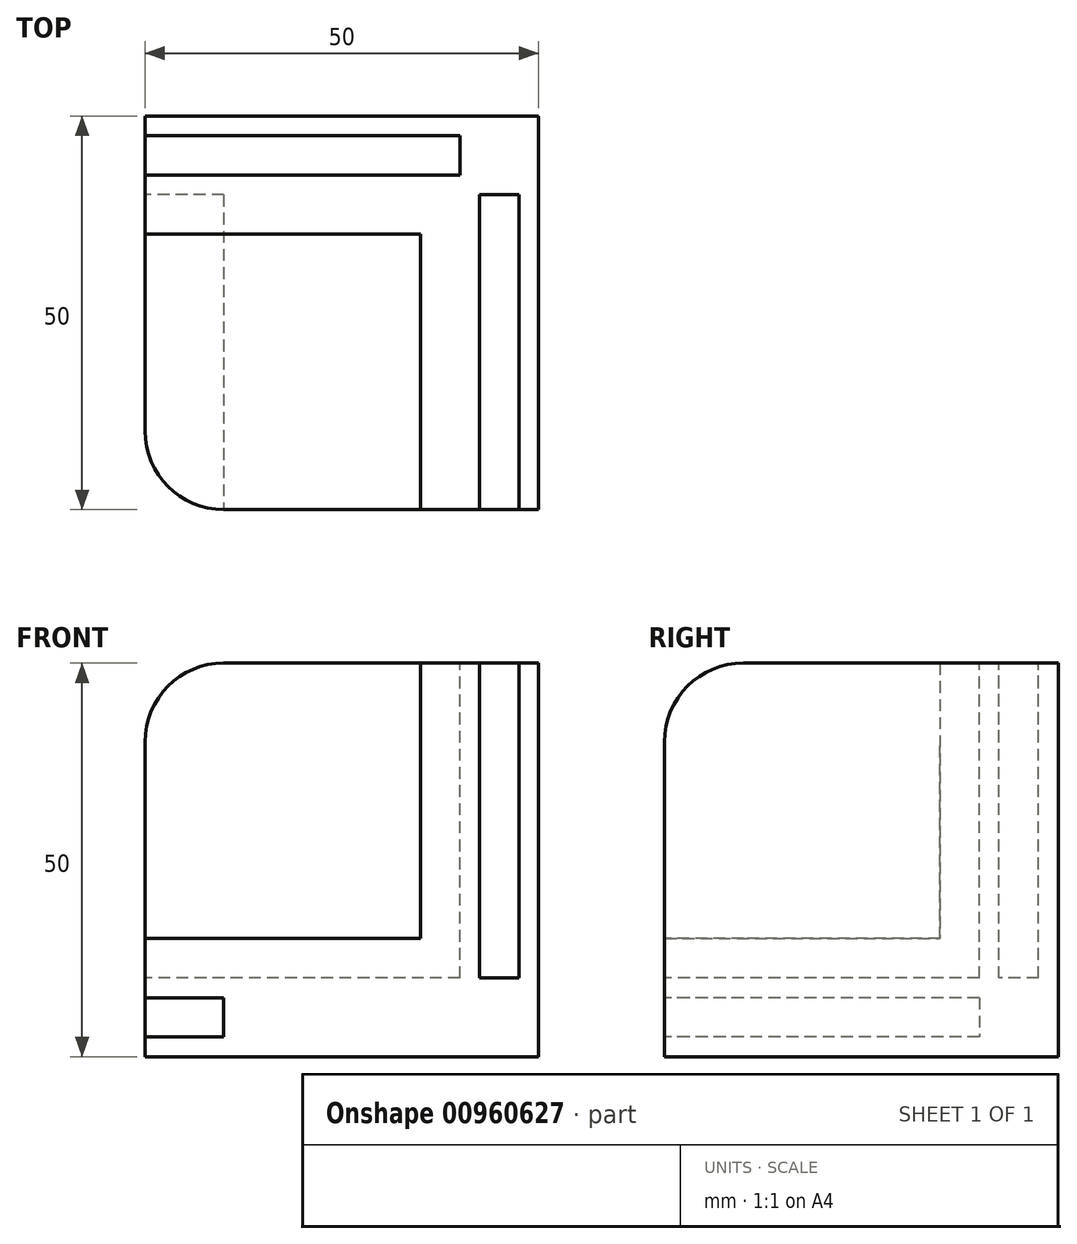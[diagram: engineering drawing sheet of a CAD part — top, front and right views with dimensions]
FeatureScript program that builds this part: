
annotation { "Feature Type Name" : "Feature", "Feature Type Description" : "" }
export const myFeature = defineFeature(function(context is Context, id is Id, definition is map)
    precondition{}
    {
        {
            var Q0;
            Q0=qCreatedBy(makeId("Top.planeOp"),FACE);
            var sketch = newSketch(context, id + "F0", { "sketchPlane" : qUnion([Q0])});
            skLineSegment(sketch, "E0.bottom", {"start": v(0, 0) * mm, "end": v(-50, 0) * mm});
            skLineSegment(sketch, "E0.top", {"start": v(0, -50) * mm, "end": v(-40, -50) * mm});
            skLineSegment(sketch, "E0.left", {"start": v(0, 0) * mm, "end": v(0, -50) * mm});
            skLineSegment(sketch, "E0.right", {"start": v(-50, 0) * mm, "end": v(-50, -40) * mm});
            skPoint(sketch, "E1.visualSharp", {"position": v(-50, -50) * mm});
            skArc(sketch, "E1.filletArc", {"start": v(-50, -40) * mm, "mid": v(-47.07, -47.07) * mm, "end": v(-40, -50) * mm});
            skSolve(sketch);
        }
        {
            var Q0;
            Q0=makeQuery(id+"F0.imprint","IMPRINT",FACE,{"disambiguationData":[TD([[makeQuery(id+"F0.imprint","IMPRINT",EDGE,{"derivedFrom":sQuery(id+"F0.wireOp",EDGE,"tNkWgY0K-5FoM-fzsk-HCrw-KOSka2LcS9h1.bottom")}),-1.0]])]});
            var Q1;
            Q1=makeQuery(id+"F0.imprint","IMPRINT",FACE,{"disambiguationData":[TD([[makeQuery(id+"F0.imprint","IMPRINT",EDGE,{"derivedFrom":sQuery(id+"F0.wireOp",EDGE,"E0.bottom")}),1.0]])]});
            var Q2;
            Q2=makeQuery(id+"F0.imprint","IMPRINT",FACE,{"disambiguationData":[TD([[makeQuery(id+"F0.imprint","IMPRINT",EDGE,{"derivedFrom":sQuery(id+"F0.wireOp",EDGE,"E0.top")}),-1.0]])]});
            var Q3;
            Q3=makeQuery(id+"F0.imprint","IMPRINT",FACE,{"disambiguationData":[TD([[makeQuery(id+"F0.imprint","IMPRINT",EDGE,{"derivedFrom":sQuery(id+"F0.wireOp",EDGE,"fvIwUqZD-S5C8-yHxi-N0ak-uGxWySerV2bo.bottom")}),1.0]])]});
            var Q4;
            Q4=makeQuery(id+"F0.imprint","IMPRINT",FACE,{"disambiguationData":[TD([[makeQuery(id+"F0.imprint","IMPRINT",EDGE,{"derivedFrom":sQuery(id+"F0.wireOp",EDGE,"JSCxDXyh-nDxv-V0qH-dKlW-7TGNpykFalIj.bottom")}),1.0]])]});
            extrude(context, id + "F1", {"entities" : qUnion([Q0, Q1, Q2, Q3, Q4]), "depth" : 15 * mm, "offsetDistance" : 25 * mm});
        }
        {
            var Q0;
            Q0=qCreatedBy(makeId("Right.planeOp"),FACE);
            var sketch = newSketch(context, id + "F2", { "sketchPlane" : qUnion([Q0])});
            skLineSegment(sketch, "E2.bottom", {"start": v(0, 10) * mm, "end": v(-50, 10) * mm});
            skLineSegment(sketch, "E2.top", {"start": v(0, 50) * mm, "end": v(-40, 50) * mm});
            skLineSegment(sketch, "E2.left", {"start": v(0, 10) * mm, "end": v(0, 50) * mm});
            skLineSegment(sketch, "E2.right", {"start": v(-50, 10) * mm, "end": v(-50, 40) * mm});
            skPoint(sketch, "E3.visualSharp", {"position": v(-50, 50) * mm});
            skArc(sketch, "E3.filletArc", {"start": v(-40, 50) * mm, "mid": v(-47.07, 47.07) * mm, "end": v(-50, 40) * mm});
            skSolve(sketch);
        }
        {
            var Q0;
            Q0=makeQuery(id+"F2.imprint","IMPRINT",FACE,{"disambiguationData":[TD([[makeQuery(id+"F2.imprint","IMPRINT",EDGE,{"derivedFrom":sQuery(id+"F2.wireOp",EDGE,"E2.bottom")}),-1.0]])]});
            extrude(context, id + "F3", {"entities" : qUnion([Q0]), "operationType" : NewBodyOperationType.ADD, "oppositeDirection" : true, "depth" : 15 * mm, "offsetDistance" : 25 * mm});
        }
        {
            var Q0;
            Q0=qCreatedBy(makeId("Front.planeOp"),FACE);
            var sketch = newSketch(context, id + "F4", { "sketchPlane" : qUnion([Q0])});
            skLineSegment(sketch, "E4.bottom", {"start": v(-10, 10) * mm, "end": v(-50, 10) * mm});
            skLineSegment(sketch, "E4.top", {"start": v(-10, 50) * mm, "end": v(-40, 50) * mm});
            skLineSegment(sketch, "E4.left", {"start": v(-10, 10) * mm, "end": v(-10, 50) * mm});
            skLineSegment(sketch, "E4.right", {"start": v(-50, 10) * mm, "end": v(-50, 40) * mm});
            skPoint(sketch, "E5.visualSharp", {"position": v(-50, 50) * mm});
            skArc(sketch, "E5.filletArc", {"start": v(-40, 50) * mm, "mid": v(-47.07, 47.07) * mm, "end": v(-50, 40) * mm});
            skSolve(sketch);
        }
        {
            var Q0;
            Q0=makeQuery(id+"F4.imprint","IMPRINT",FACE,{"disambiguationData":[TD([[makeQuery(id+"F4.imprint","IMPRINT",EDGE,{"derivedFrom":sQuery(id+"F4.wireOp",EDGE,"E4.bottom")}),-1.0]])]});
            extrude(context, id + "F5", {"entities" : qUnion([Q0]), "operationType" : NewBodyOperationType.ADD, "depth" : 15 * mm, "offsetDistance" : 25 * mm});
        }
        {
            var Q0;
            Q0=makeQuery(id+"F3.boolean.opBoolean","MERGE",FACE,{"derivedFrom":[makeQuery(id+"F1.opExtrude","SWEPT_FACE",FACE,{"disambiguationData":[OSD([sQuery(id+"F0.wireOp",EDGE,"E0.top")])]}),makeQuery(id+"F3.opExtrude","SWEPT_FACE",FACE,{"disambiguationData":[OSD([sQuery(id+"F2.wireOp",EDGE,"E2.right")])]})]});
            var sketch = newSketch(context, id + "F6", { "sketchPlane" : qUnion([Q0])});
            skLineSegment(sketch, "E6.bottom", {"start": v(-10, 2.5) * mm, "end": v(-60, 2.5) * mm});
            skLineSegment(sketch, "E6.top", {"start": v(-10, 7.5) * mm, "end": v(-60, 7.5) * mm});
            skLineSegment(sketch, "E6.left", {"start": v(-10, 2.5) * mm, "end": v(-10, 7.5) * mm});
            skLineSegment(sketch, "E6.right", {"start": v(-60, 2.5) * mm, "end": v(-60, 7.5) * mm});
            skLineSegment(sketch, "E7.bottom", {"start": v(-10, 2.5) * mm, "end": v(-15, 2.5) * mm});
            skLineSegment(sketch, "E7.top", {"start": v(-10, 52.5) * mm, "end": v(-15, 52.5) * mm});
            skLineSegment(sketch, "E8.bottom", {"start": v(-2.5, 10) * mm, "end": v(-7.5, 10) * mm});
            skLineSegment(sketch, "E8.top", {"start": v(-2.5, 60) * mm, "end": v(-7.5, 60) * mm});
            skLineSegment(sketch, "E8.left", {"start": v(-2.5, 10) * mm, "end": v(-2.5, 60) * mm});
            skLineSegment(sketch, "E8.right", {"start": v(-7.5, 10) * mm, "end": v(-7.5, 60) * mm});
            skSolve(sketch);
        }
        {
            var Q0;
            {var subQ5=sQuery(id+"F6.wireOp",EDGE,"E7.bottom");Q0=makeQuery(id+"F6.imprint","IMPRINT",FACE,{"disambiguationData":[TD([[makeQuery(id+"F6.imprint","IMPRINT",EDGE,{"derivedFrom":subQ5}),-1.0]])]});}
            var Q1;
            {var subQ0=sQuery(id+"F6.wireOp",EDGE,"E7.right");var subQ5=sQuery(id+"F6.wireOp",EDGE,"E6.top");var subQ7=makeQuery(id+"F6.imprint","INTERSECT",VERTEX,{"derivedFrom":[subQ5,subQ0]});Q1=makeQuery(id+"F6.imprint","IMPRINT",FACE,{"disambiguationData":[TD([[makeQuery(id+"F6.imprint","IMPRINT",EDGE,{"disambiguationData":[TD([[subQ7,-1.0]])],"derivedFrom":subQ5}),1.0]])]});}
            var Q2;
            {var subQ0=sQuery(id+"F6.wireOp",EDGE,"E6.right");Q2=makeQuery(id+"F6.imprint","IMPRINT",FACE,{"disambiguationData":[TD([[makeQuery(id+"F6.imprint","IMPRINT",EDGE,{"derivedFrom":subQ0}),-1.0]])]});}
            var Q3;
            {var subQ0=sQuery(id+"F6.wireOp",EDGE,"E8.bottom");Q3=makeQuery(id+"F6.imprint","IMPRINT",FACE,{"disambiguationData":[TD([[makeQuery(id+"F6.imprint","IMPRINT",EDGE,{"derivedFrom":subQ0}),-1.0]])]});}
            var Q4;
            {var subQ0=sQuery(id+"F6.wireOp",EDGE,"E8.top");Q4=makeQuery(id+"F6.imprint","IMPRINT",FACE,{"disambiguationData":[TD([[makeQuery(id+"F6.imprint","IMPRINT",EDGE,{"derivedFrom":subQ0}),1.0]])]});}
            extrude(context, id + "F7", {"entities" : qUnion([Q0, Q1, Q2, Q3, Q4]), "operationType" : NewBodyOperationType.REMOVE, "oppositeDirection" : true, "depth" : 40 * mm, "offsetDistance" : 25 * mm});
        }
        {
            var Q0;
            Q0=makeQuery(id+"F5.boolean.opBoolean","MERGE",FACE,{"derivedFrom":[makeQuery(id+"F3.opExtrude","SWEPT_FACE",FACE,{"disambiguationData":[OSD([sQuery(id+"F2.wireOp",EDGE,"E2.top")])]}),makeQuery(id+"F5.opExtrude","SWEPT_FACE",FACE,{"disambiguationData":[OSD([sQuery(id+"F4.wireOp",EDGE,"E4.top")])]})]});
            var sketch = newSketch(context, id + "F8", { "sketchPlane" : qUnion([Q0])});
            skLineSegment(sketch, "E9.bottom", {"start": v(-10, -2.5) * mm, "end": v(-60, -2.5) * mm});
            skLineSegment(sketch, "E9.top", {"start": v(-10, -7.5) * mm, "end": v(-60, -7.5) * mm});
            skLineSegment(sketch, "E9.left", {"start": v(-10, -2.5) * mm, "end": v(-10, -7.5) * mm});
            skLineSegment(sketch, "E9.right", {"start": v(-60, -2.5) * mm, "end": v(-60, -7.5) * mm});
            skSolve(sketch);
        }
        {
            var Q0;
            {var subQ0=sQuery(id+"F8.wireOp",EDGE,"E9.left");Q0=makeQuery(id+"F8.imprint","IMPRINT",FACE,{"disambiguationData":[TD([[makeQuery(id+"F8.imprint","IMPRINT",EDGE,{"derivedFrom":subQ0}),-1.0]])]});}
            var Q1;
            {var subQ0=sQuery(id+"F8.wireOp",EDGE,"E9.right");Q1=makeQuery(id+"F8.imprint","IMPRINT",FACE,{"disambiguationData":[TD([[makeQuery(id+"F8.imprint","IMPRINT",EDGE,{"derivedFrom":subQ0}),1.0]])]});}
            extrude(context, id + "F9", {"entities" : qUnion([Q0, Q1]), "operationType" : NewBodyOperationType.REMOVE, "oppositeDirection" : true, "depth" : 40 * mm, "offsetDistance" : 25 * mm});
        }
    });
